# Revit family: Shower-Valve_Trim-KOHLER-Fore_Tri-K-38163T
name_source: partatom
category: Plumbing Fixtures
units: mm (PartAtom-declared; Revit-internal decimal feet)

## family parameters
Cut with Voids When Loaded = No
Host = Face
Maintain Annotation Orientation = No
OmniClass Number = 23.31.25.00
OmniClass Title = Toilet and Bath Specialties
Part Type = Normal
Room Calculation Point = No
Round Connector Dimension = Use Diameter
Shared = No

## types (3) — shared parameters
ADA Compliant = No
Assembly Code = C1030200
CW Connection = Yes
Cold Water Inlet = Cold Water Inlet
Cold Water Outlet = Cold Water Outlet
Date Modified = 03/27/2025
Default Elevation = 42"
Description = Exposed Shower Valve Cold
HW Connection = No
Handle Clearance = 3 3/16"
Height = 3 15/16"
Hot Water Inlet = Hot Water Inlet
Length = 4 1/8"
Manufacturer = Kohler Co.
Master Format 2014 = 10 28 00
Master Format 2014 Name = Toilet, Bath, and Laundry Accessories
Material = Premium Metal Construction
Product Name = Fore Tri
URL = http://www.kohler.com.cn
Vent Connection = No
Waste Connection = No
WaterSense Certified = No
Width = 3 15/16"

## per-type parameters (varying)
| type | Finish | Model | Type |
| AF-Vibrant French Gold | Kohler-Metal-AF-Vibrant_French_Gold | K-38163T-4CD-AF | 1 |
| BL-Matte Black | Kohler-Metal-BL-Matte_Black | K-38163T-4CD-BL | 2 |
| CP-Polished Chrome | Kohler-Metal-CP-Polished_Chrome | K-38163T-4CD-CP | 3 |

## geometry (parser evidence)
native form markers: Sweep x5
no freeform markers — native parametric forms only
